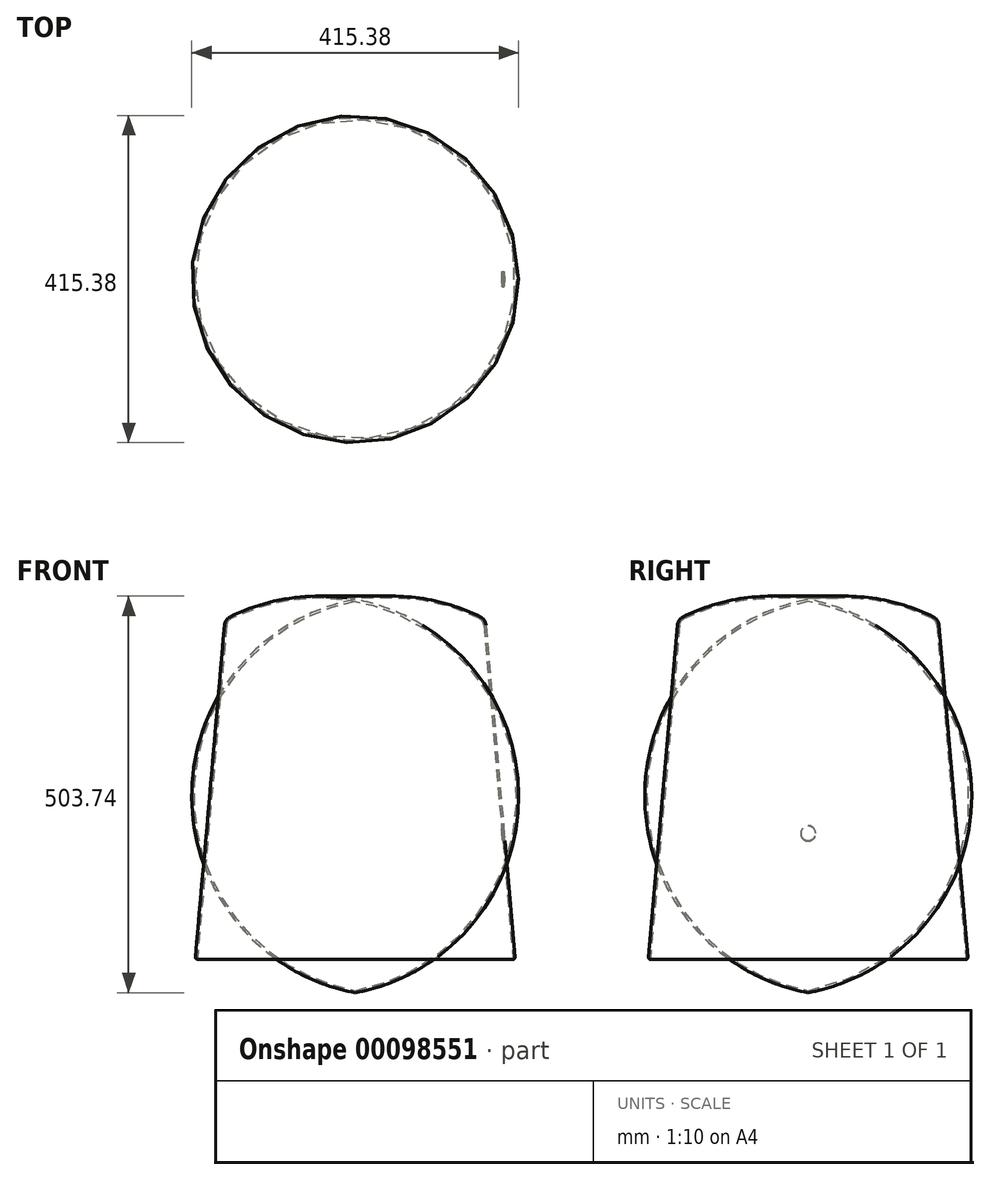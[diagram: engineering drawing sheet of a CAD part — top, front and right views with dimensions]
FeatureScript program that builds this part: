
annotation { "Feature Type Name" : "Feature", "Feature Type Description" : "" }
export const myFeature = defineFeature(function(context is Context, id is Id, definition is map)
    precondition{}
    {
        {
            var Q0;
            Q0=qCreatedBy(makeId("Front.planeOp"),FACE);
            var sketch = newSketch(context, id + "F0", { "sketchPlane" : qUnion([Q0])});
            skLineSegment(sketch, "E0", {"start": v(0, 0) * mm, "end": v(-203.2, 0) * mm});
            skLineSegment(sketch, "E1", {"start": v(0, 0) * mm, "end": v(0, 457.2) * mm});
            skLineSegment(sketch, "E2", {"start": v(-203.2, 0) * mm, "end": v(-166.03, 424.81) * mm});
            skArc(sketch, "E3", {"start": v(0, 457.2) * mm, "mid": v(-81.3, 459.04) * mm, "end": v(-159.02, 435.09) * mm});
            skArc(sketch, "E4", {"start": v(-159.02, 435.09) * mm, "mid": v(-163.87, 430.87) * mm, "end": v(-166.03, 424.81) * mm});
            skPoint(sketch, "E5.orphan", {"position": v(-165.42, 431.8) * mm});
            skSolve(sketch);
        }
        {
            var Q0;
            Q0=makeQuery(id+"F0.imprint","IMPRINT",FACE,{"disambiguationData":[TD([[makeQuery(id+"F0.imprint","IMPRINT",EDGE,{"derivedFrom":sQuery(id+"F0.wireOp",EDGE,"E0")}),-1.0]])]});
            var Q1;
            Q1=sQuery(id+"F0.wireOp",EDGE,"E1");
            revolve(context, id + "F1", {"entities" : qUnion([Q0]), "axis" : qUnion([Q1]), "revolveType" : RevolveType.FULL});
        }
        {
            var Q0;
            Q0=makeQuery(id+"F1.opRevolve","SWEPT_FACE",FACE,{"disambiguationData":[OSD([sQuery(id+"F0.wireOp",EDGE,"E0")])]});
            shell(context, id + "F2", {"entities" : qUnion([Q0]), "thickness" : 2.54 * mm});
        }
        {
            var Q0;
            Q0=makeQuery(id+"F1.opRevolve","SWEPT_EDGE",EDGE,{"disambiguationData":[OSD([sQuery(id+"F0.wireOp",EDGE,"E0"),sQuery(id+"F0.wireOp",EDGE,"E2")])]});
            fillet(context, id + "F3", {"entities" : qUnion([Q0]), "radius" : 3.17 * mm, "tangentPropagation" : true, "allowEdgeOverflow" : false});
        }
        {
            var Q0;
            {var subQ0=sQuery(id+"F0.wireOp",EDGE,"E2");Q0=makeQuery(id+"F3.opFillet","BLEND_EDGE",EDGE,{"blendedFrom":[makeQuery(id+"F1.opRevolve","SWEPT_EDGE",EDGE,{"disambiguationData":[OSD([sQuery(id+"F0.wireOp",EDGE,"E0"),subQ0])]}),makeQuery(id+"F2.opShell","OFFSET_FACE",FACE,{"disambiguationData":[OSD([subQ0])]})],"blendedInto":[makeQuery(id+"F2.opShell","OFFSET_FACE",FACE,{"disambiguationData":[OSD([subQ0])]})]});}
            fillet(context, id + "F4", {"entities" : qUnion([Q0]), "radius" : 0.5 * mm, "tangentPropagation" : true, "allowEdgeOverflow" : false});
        }
        {
            var Q0;
            Q0=qCreatedBy(makeId("Front.planeOp"),FACE);
            var sketch = newSketch(context, id + "F5", { "sketchPlane" : qUnion([Q0])});
            skLineSegment(sketch, "E6", {"start": v(0, 0) * mm, "end": v(0, 127) * mm, "construction": true});
            skLineSegment(sketch, "E7", {"start": v(0, 127) * mm, "end": v(200.11, 162.29) * mm, "construction": true});
            skSolve(sketch);
        }
        {
            var Q0;
            Q0=sQuery(id+"F5.wireOp",VERTEX,"E7.end");
            var Q1;
            Q1=sQuery(id+"F5.wireOp",EDGE,"E7");
            cPlane(context, id + "F6", {"entities" : qUnion([Q0, Q1]), "cplaneType" : CPlaneType.LINE_POINT, "offset" : 152.4 * mm, "width" : 152.4 * mm, "height" : 152.4 * mm});
        }
        {
            var Q0;
            Q0=qCreatedBy(id+"F6.planeOp",FACE);
            var sketch = newSketch(context, id + "F7", { "sketchPlane" : qUnion([Q0])});
            skCircle(sketch, "E8", {"center": v(0, 125.07) * mm, "radius": 9.53 * mm});
            skSolve(sketch);
        }
        {
            var Q0;
            Q0=makeQuery(id+"F7.imprint","IMPRINT",FACE,{"disambiguationData":[TD([[makeQuery(id+"F7.imprint","IMPRINT",EDGE,{"derivedFrom":sQuery(id+"F7.wireOp",EDGE,"E8")}),1.0]])]});
            extrude(context, id + "F8", {"entities" : qUnion([Q0]), "operationType" : NewBodyOperationType.REMOVE, "oppositeDirection" : true, "depth" : 127 * mm});
        }
    });
